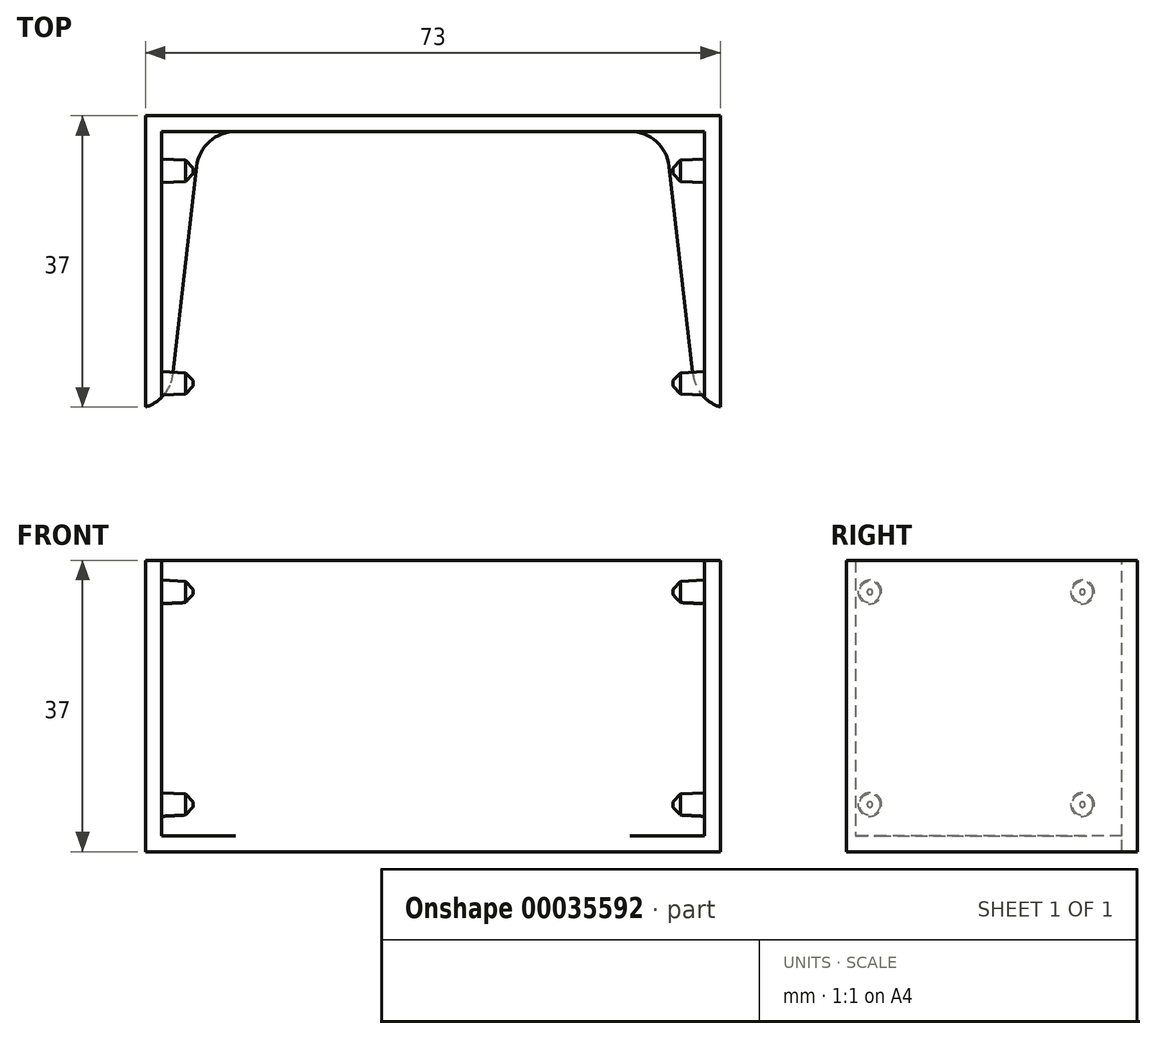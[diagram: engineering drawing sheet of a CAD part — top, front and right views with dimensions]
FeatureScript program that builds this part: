
annotation { "Feature Type Name" : "Feature", "Feature Type Description" : "" }
export const myFeature = defineFeature(function(context is Context, id is Id, definition is map)
    precondition{}
    {
        {
            var Q0;
            Q0=qCreatedBy(makeId("Front.planeOp"),FACE);
            var sketch = newSketch(context, id + "F0", { "sketchPlane" : qUnion([Q0])});
            skLineSegment(sketch, "E0.rect.bottom", {"start": v(34.5, -17.5) * mm, "end": v(-34.5, -17.5) * mm});
            skLineSegment(sketch, "E0.rect.top", {"start": v(34.5, 17.5) * mm, "end": v(-34.5, 17.5) * mm});
            skLineSegment(sketch, "E0.rect.left", {"start": v(34.5, -17.5) * mm, "end": v(34.5, 17.5) * mm});
            skLineSegment(sketch, "E0.rect.right", {"start": v(-34.5, -17.5) * mm, "end": v(-34.5, 17.5) * mm});
            skPoint(sketch, "E0.rect.middle", {"position": v(0, 0) * mm});
            skSolve(sketch);
        }
        {
            var Q0;
            Q0 = qSketchRegion(id + "F0", true);
            extrude(context, id + "F1", {"entities" : qUnion([Q0]), "oppositeDirection" : true, "depth" : 2 * mm});
        }
        {
            var Q0;
            Q0=makeQuery(id+"F1.opExtrude","SWEPT_FACE",FACE,{"disambiguationData":[OSD([sQuery(id+"F0.wireOp",EDGE,"E0.rect.left")])]});
            var sketch = newSketch(context, id + "F2", { "sketchPlane" : qUnion([Q0])});
            skLineSegment(sketch, "E1.bottom", {"start": v(2, 17.5) * mm, "end": v(-35, 17.5) * mm});
            skLineSegment(sketch, "E1.top", {"start": v(2, -17.5) * mm, "end": v(-35, -17.5) * mm});
            skLineSegment(sketch, "E1.left", {"start": v(2, 17.5) * mm, "end": v(2, -17.5) * mm});
            skLineSegment(sketch, "E1.right", {"start": v(-35, 17.5) * mm, "end": v(-35, -17.5) * mm});
            skSolve(sketch);
        }
        {
            var Q0;
            Q0 = qSketchRegion(id + "F2", true);
            extrude(context, id + "F3", {"entities" : qUnion([Q0]), "operationType" : NewBodyOperationType.ADD, "depth" : 2 * mm});
        }
        {
            var Q0;
            Q0=makeQuery(id+"F3.opExtrude","CAP_FACE",FACE,{"disambiguationData":[OSD([sQuery(id+"F2.wireOp",EDGE,"E1.bottom"),sQuery(id+"F2.wireOp",EDGE,"E1.top"),sQuery(id+"F2.wireOp",EDGE,"E1.left"),sQuery(id+"F2.wireOp",EDGE,"E1.right")])],"isStart":true});
            var sketch = newSketch(context, id + "F4", { "sketchPlane" : qUnion([Q0])});
            skLineSegment(sketch, "E2.rect.bottom", {"start": v(32, -13.5) * mm, "end": v(5, -13.5) * mm, "construction": true});
            skLineSegment(sketch, "E2.rect.top", {"start": v(32, 13.5) * mm, "end": v(5, 13.5) * mm, "construction": true});
            skLineSegment(sketch, "E2.rect.left", {"start": v(32, -13.5) * mm, "end": v(32, 13.5) * mm, "construction": true});
            skLineSegment(sketch, "E2.rect.right", {"start": v(5, -13.5) * mm, "end": v(5, 13.5) * mm, "construction": true});
            skPoint(sketch, "E2.rect.middle", {"position": v(18.5, 0) * mm});
            skCircle(sketch, "E3", {"center": v(5, 13.5) * mm, "radius": 1.5 * mm});
            skCircle(sketch, "E4", {"center": v(32, 13.5) * mm, "radius": 1.5 * mm});
            skCircle(sketch, "E5", {"center": v(32, -13.5) * mm, "radius": 1.5 * mm});
            skCircle(sketch, "E6", {"center": v(5, -13.5) * mm, "radius": 1.5 * mm});
            skSolve(sketch);
        }
        {
            var Q0;
            Q0 = qSketchRegion(id + "F4", true);
            extrude(context, id + "F5", {"entities" : qUnion([Q0]), "operationType" : NewBodyOperationType.ADD, "depth" : 4 * mm, "hasDraft" : true, "draftAngle" : 3 * degree, "draftPullDirection" : true});
        }
        {
            var Q0;
            Q0=makeQuery(id+"F5.opExtrude","CAP_FACE",FACE,{"disambiguationData":[OSD([sQuery(id+"F4.wireOp",EDGE,"E3")])],"isStart":false});
            var Q1;
            Q1=makeQuery(id+"F5.opExtrude","CAP_FACE",FACE,{"disambiguationData":[OSD([sQuery(id+"F4.wireOp",EDGE,"E4")])],"isStart":false});
            var Q2;
            Q2=makeQuery(id+"F5.opExtrude","CAP_FACE",FACE,{"disambiguationData":[OSD([sQuery(id+"F4.wireOp",EDGE,"E6")])],"isStart":false});
            var Q3;
            Q3=makeQuery(id+"F5.opExtrude","CAP_FACE",FACE,{"disambiguationData":[OSD([sQuery(id+"F4.wireOp",EDGE,"E5")])],"isStart":false});
            chamfer(context, id + "F6", {"entities" : qUnion([Q0, Q1, Q2, Q3]), "width" : 1 * mm, "tangentPropagation" : true});
        }
        {
            var Q0;
            Q0=makeQuery(id+"F3.boolean.opBoolean","MERGE",FACE,{"derivedFrom":[makeQuery(id+"F1.opExtrude","SWEPT_FACE",FACE,{"disambiguationData":[OSD([sQuery(id+"F0.wireOp",EDGE,"E0.rect.bottom")])]}),makeQuery(id+"F3.opExtrude","SWEPT_FACE",FACE,{"disambiguationData":[OSD([sQuery(id+"F2.wireOp",EDGE,"E1.top")])]})]});
            var sketch = newSketch(context, id + "F7", { "sketchPlane" : qUnion([Q0])});
            skLineSegment(sketch, "E7", {"start": v(34.5, 35) * mm, "end": v(33.5, 35) * mm});
            skLineSegment(sketch, "E8", {"start": v(33.5, 35) * mm, "end": v(29.5, 0) * mm});
            skSolve(sketch);
        }
        {
            var Q0;
            Q0 = qSketchRegion(id + "F7", true);
            var Q1;
            {var subQ3=sQuery(id+"F2.wireOp",EDGE,"E1.top");Q1=makeQuery(id+"F7.imprint","IMPRINT",FACE,{"disambiguationData":[TD([[makeQuery(id+"F7.imprint","IMPRINT",EDGE,{"derivedFrom":makeQuery(id+"F3.opExtrude","CAP_EDGE",EDGE,{"disambiguationData":[OSD([subQ3])],"isStart":false})}),1.0]])]});}
            var Q2;
            Q2=makeQuery(id+"F7.imprint","IMPRINT",FACE,{"disambiguationData":[TD([[makeQuery(id+"F7.imprint","IMPRINT",EDGE,{"derivedFrom":sQuery(id+"F7.wireOp",EDGE,"E7")}),1.0]])]});
            extrude(context, id + "F8", {"entities" : qUnion([Q0, Q1, Q2]), "operationType" : NewBodyOperationType.ADD, "depth" : 2 * mm});
        }
        {
            var Q0;
            Q0=makeQuery(id+"F8.opExtrude","SWEPT_EDGE",EDGE,{"disambiguationData":[OSD([sQuery(id+"F7.wireOp",EDGE,"E7"),sQuery(id+"F7.wireOp",EDGE,"E8")])]});
            var Q1;
            Q1=makeQuery(id+"F8.opExtrude","SWEPT_EDGE",EDGE,{"disambiguationData":[OSD([sQuery(id+"F0.wireOp",EDGE,"E0.rect.bottom"),sQuery(id+"F7.wireOp",EDGE,"E8")])]});
            fillet(context, id + "F9", {"entities" : qUnion([Q0, Q1]), "radius" : 5 * mm, "tangentPropagation" : true, "allowEdgeOverflow" : false});
        }
        {
            var Q0;
            Q0=makeQuery(id+"F1.opExtrude","SWEPT_BODY",BODY,{"disambiguationData":[OSD([sQuery(id+"F0.wireOp",EDGE,"E0.rect.bottom"),sQuery(id+"F0.wireOp",EDGE,"E0.rect.top"),sQuery(id+"F0.wireOp",EDGE,"E0.rect.left"),sQuery(id+"F0.wireOp",EDGE,"E0.rect.right")])]});
            var Q1;
            Q1=qCreatedBy(makeId("Right.planeOp"),FACE);
            mirror(context, id + "F10", {"operationType" : NewBodyOperationType.ADD, "entities" : qUnion([Q0]), "mirrorPlane" : qUnion([Q1])});
        }
    });
